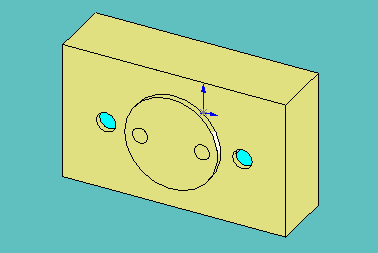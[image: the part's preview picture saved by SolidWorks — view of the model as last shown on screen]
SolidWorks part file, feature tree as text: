
SOLIDWORKS PART (.sldprt)
format: sldprt  version: not decoded by parser v0  size: 271,360 bytes
history: native  units: mm
features: sketch x5, extrude x4, material x1, plane x1, cut_extrude x1 (+11 scaffold rows collapsed)
feature tree (23):
  scaffold x11  (default folders/planes/origin — collapsed)
  material  "Material <not specified>"
  sketch  "Sketch1"  dims[D1=~76.17529mm]
  extrude  "Extrude1"  Depth=6.35mm
  extrude  "Extrude2"  [1 undecoded]
  sketch  "Sketch1<3>"  dims[D1=50.8mm]
  plane  "Plane1"  Offset=50.8mm
  extrude  "Extrude4"  [1 undecoded]
  sketch  "Sketch1<6>"  dims[D1=63.5mm]
  sketch  "Sketch16"
  extrude  "Extrude3"  Depth=6.35mm
  cut_extrude  "Cut-Extrude2"  [1 undecoded]
  sketch  "Sketch1<5>"  dims[D1=57.15mm]
decode coverage: 6 of 10 modeling features carry decoded parameters
note: ~ marks probable driven/reference dimensions
note: 3 parameter values undecoded
summary: no parameter record found for 3 features
note: suppression state not decoded; provenance and decode notes live in map.json
